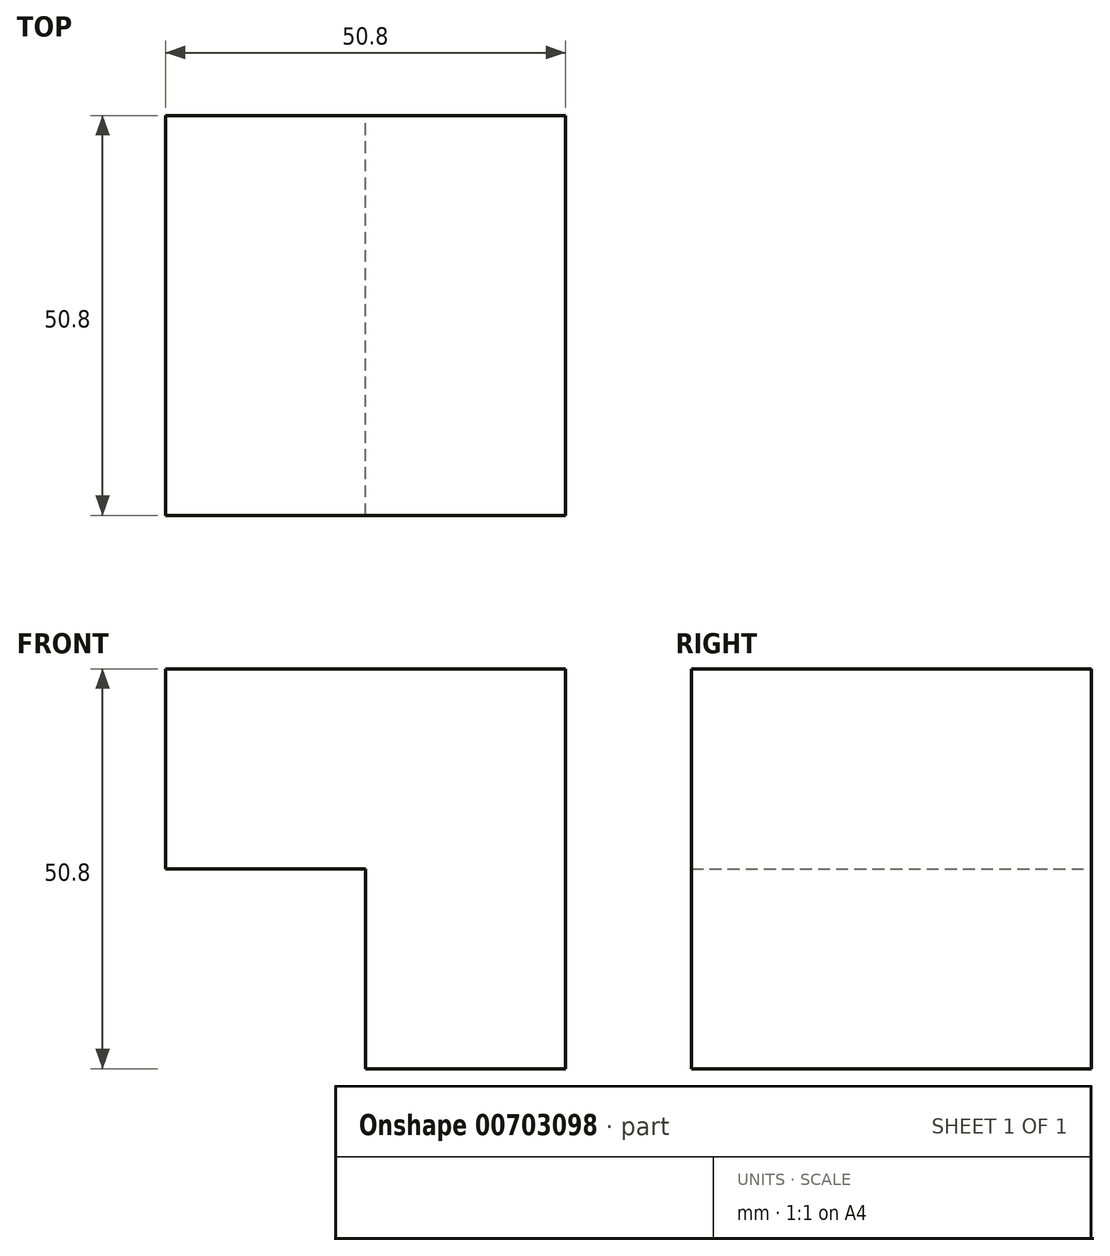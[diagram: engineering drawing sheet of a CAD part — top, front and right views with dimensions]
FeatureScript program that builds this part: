
annotation { "Feature Type Name" : "Feature", "Feature Type Description" : "" }
export const myFeature = defineFeature(function(context is Context, id is Id, definition is map)
    precondition{}
    {
        {
            var Q0;
            Q0=qCreatedBy(makeId("Front.planeOp"),FACE);
            var sketch = newSketch(context, id + "F0", { "sketchPlane" : qUnion([Q0])});
            skLineSegment(sketch, "E0", {"start": v(-25.4, 25.4) * mm, "end": v(25.4, 25.4) * mm});
            skLineSegment(sketch, "E1", {"start": v(25.4, 25.4) * mm, "end": v(25.4, -25.4) * mm});
            skLineSegment(sketch, "E2", {"start": v(25.4, -25.4) * mm, "end": v(0, -25.4) * mm});
            skLineSegment(sketch, "E3", {"start": v(0, -25.4) * mm, "end": v(0, 0) * mm});
            skLineSegment(sketch, "E4", {"start": v(0, 0) * mm, "end": v(-25.4, 0) * mm});
            skLineSegment(sketch, "E5", {"start": v(-25.4, 25.4) * mm, "end": v(-25.4, 0) * mm});
            skSolve(sketch);
        }
        {
            var Q0;
            Q0=makeQuery(id+"F0.imprint","IMPRINT",FACE,{"disambiguationData":[TD([[makeQuery(id+"F0.imprint","IMPRINT",EDGE,{"derivedFrom":sQuery(id+"F0.wireOp",EDGE,"E0")}),-1.0]])]});
            extrude(context, id + "F1", {"entities" : qUnion([Q0]), "depth" : 50.8 * mm, "offsetDistance" : 25.4 * mm});
        }
    });
